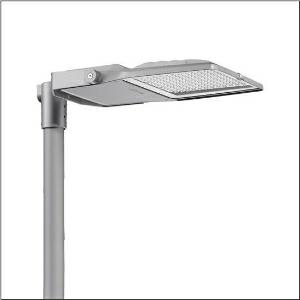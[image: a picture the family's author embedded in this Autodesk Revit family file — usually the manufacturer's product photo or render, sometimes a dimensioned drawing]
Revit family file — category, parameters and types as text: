
# Revit family: floodlight_fl_21_iq_midi___pl52_5xa7782f4d3a_fe87
name_source: partatom
category: Lighting Fixtures
units: mm (PartAtom-declared; Revit-internal decimal feet)

## family parameters
Cut with Voids When Loaded = No
Host = Face
Light Source = No
Part Type = Normal
Room Calculation Point = No
Round Connector Dimension = Use Diameter
Shared = No

## types (1)
- --- (1 x LED, 37330 lm, 270.2 W, 4000K)
    Apparent Load = 270 VA
    CIE Flux Codes = 26 60 98 100 100
    Color Rendering = 70
    Color Temperature = 4000K
    Default Elevation = 1800 mm
    Description = Floodlight FL 21 iQ midi, floodlight, primary light control with lens, of PMMA, primary optical cover: protective disc, of toughened safety glass, transparent, light distribution: PL52, light emission: direct distribution, installation type: surface-mounted, LED, High Power LED, rated luminous flux: 37.330lm, luminous efficacy: 138lm/W, light colour: 740, colour temperature: 4000K, control gear: iQ Street-Remote/DALI, control: optimised constant luminous flux control (CLO 2.0), Desk-Remote (wireless, voltage-free reading and setting of iQ features in the workshop via application-optimized NFC function/RFID function), Smart-Wire, Night-Set, Temp-Guard, Auto-Match, Street-Remote, with terminal, 6-pole, mains connection: 220..240V, AC, 50/60Hz, start of lifetime: 270W, end of service life: 287W, reduction: 118W, luminaire housing, of diecast aluminium, powder-coated, Siteco® metallic grey (DB 702S), corrosivity category C5 mid according to DIN EN ISO 12944, suitable for swimming pools, chlorine-resistant, sealing non-destructively replaceable, please order mast flange separately, mast bracket, of steel, galvanised, powder-coated, Siteco® metallic grey (DB 702S), protection rating (complete): IP66, insulation class (complete): insulation class II (safety insulation), certification: CE, ENEC, VDE, protection symbol: D, impact resistance: IK08, permissible operating ambient temperature: -40..+40°C, permissible operating ambient temperature for outdoor applications: -40..+50°C, standard: DIN EN 12944, LABS conformity tested according to VDMA 24364:2018-05, packaging unit: 1 piece

Light Distribution: PL52
    Height = 76 mm
    Lamp = 1 x LED
    Lamp Light Flux = 37330 lm
    Lamp Power = 270.2 W
    Lamp count = 1
    Length = 657 mm
    Luminous efficacy = 138 lm/W
    Manufacturer = Siteco
    ModVariant = No
    Model = 5XA7782F4D3A
    Number of Poles = 1
    OnlyDefault = Yes
    Power Factor = 1
    Product Name = Floodlight FL 21 iQ midi | PL52
    Product group = floodlight | pylon annexe
    ProductGroupID = 6201
    Protection Class = Protection class II
    Protection Degree = IP 66
    RLX_Detail_Level = 1
    RLX_Emergency_Light_Flux = 0 lm
    RLX_Emergency_Type = 0
    RLX_Emergency_Type_DB = No
    RlxData = <blob elided: 153725 chars, md5=678e8691>
    Socket = socket
    Standby Power = 0 W
    System Light Flux = 37330 lm
    System Power = 270 W
    Type Comments = factory setting: luminous flux: 100 % | dim-lin: 254 | 620 mA
    Type Image = l_1007123.jpg
    URL = http://relux.com
    VarID = @adj_126955
    Voltage = 0 V
    Weight = 0.00 kg
    Width = 442 mm

## geometry (parser evidence)
native form markers: Blend x4, Sweep x11
no freeform markers — native parametric forms only
